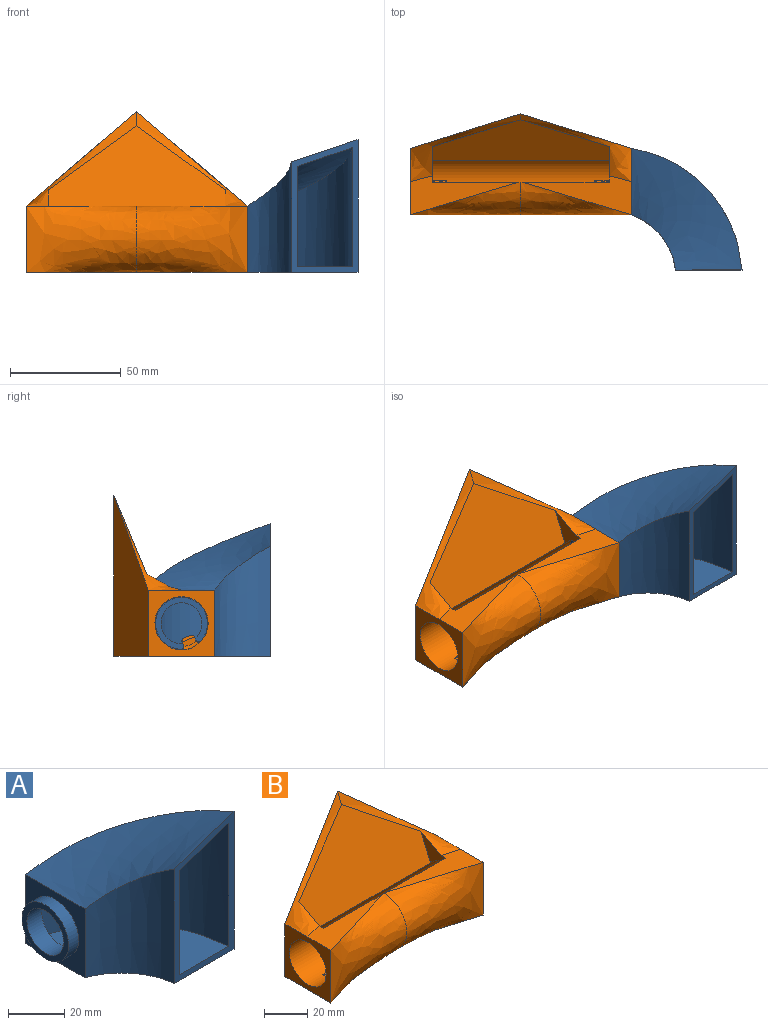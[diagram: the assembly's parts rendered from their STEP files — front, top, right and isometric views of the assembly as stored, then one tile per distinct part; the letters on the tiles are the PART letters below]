
ASSEMBLY  parts=2 mates=1
PART A: 14 faces, bbox 60x60.4x65 mm
  f0: plane 60.52x30.52mm, normal (0,-1,0), area 411.1mm2, adj f2,f3,f4,f5,f9,f10,f11,f12
  f1: plane 30x30mm, normal (-1,0,0), area 466.3mm2, adj f2,f3,f4,f5,f6
  f2: bspline ~50.26x25.43mm, area 1347.3mm2, adj f0,f1,f3,f5
  f3: bspline ~55x50mm, area 1873.7mm2, adj f0,f1,f2,f4
  f4: bspline ~60x55mm, area 3610.5mm2, adj f0,f1,f3,f5
  f5: plane 55x50mm, normal (0,0,-1), area 1683.7mm2, adj f0,f1,f2,f4
  f6: cylinder r=11.75mm len=23.5mm, axis (1,0,0), area 369.1mm2, adj f1,f7
  f7: plane 23.5x23.5mm, normal (-1,0,0), area 164.9mm2, adj f6,f13
  f8: plane 26.26x25.38mm, normal (1,0,0), area 384mm2, adj f9,f10,f11,f12,f13
  f9: offset ~55.26x30.43mm, area 1241.1mm2, adj f0,f8,f10,f12
  f10: offset ~60x55mm, area 1480.6mm2, adj f0,f8,f9,f11
  f11: offset ~65x60mm, area 2913.6mm2, adj f0,f8,f10,f12
  f12: plane 52.63x45.76mm, normal (0,0,1), area 1336.4mm2, adj f0,f8,f9,f11
  f13: cylinder r=9.25mm len=18.5mm, axis (1,0,0), area 435.9mm2, adj f7,f8
PART B: 42 faces, bbox 100x45.5x72.7 mm
  f0: cylinder r=12mm len=100mm, axis (1,0,0), area 6407mm2, adj f4,f9,f12,f13,f14,f15,f34,f35
  f1: bspline ~50x42.69mm, area 363.1mm2, adj f2,f3,f4,f8,f12,f14
  f2: plane 49.17x17.55mm, normal (0,0,1), area 377.9mm2, adj f1,f4,f6,f13,f14
  f3: bspline ~50x42.69mm, area 363.1mm2, adj f1,f5,f9,f11,f12,f15
  f4: plane 30x30mm, normal (-1,0,0), area 447.6mm2, adj f0,f1,f2,f6,f7,f8
  f5: plane 49.17x17.55mm, normal (0,0,1), area 377.9mm2, adj f3,f9,f10,f13,f15
  f6: bspline ~50x30mm, area 1813.5mm2, adj f2,f4,f7,f10,f13
  f7: plane 100x45.54mm, normal (0,0,-1), area 3026.9mm2, adj f4,f6,f8,f9,f10,f11
  f8: plane 72.69x50mm, normal (-0.3,0.95,0), area 2688.4mm2, adj f1,f4,f7,f11
  f9: plane 30x30mm, normal (1,0,0), area 447.6mm2, adj f0,f3,f5,f7,f10,f11
  f10: bspline ~50x30mm, area 1813.5mm2, adj f5,f6,f7,f9,f13
  f11: plane 72.69x50mm, normal (0.3,0.95,0), area 2688.4mm2, adj f3,f7,f8,f9
  f12: plane 80x44mm, normal (0,-0.92,0.38), area 2555.6mm2, adj f0,f1,f3,f14,f15
  f13: plane 80x3.1mm, normal (0,0.92,-0.38), area 268.6mm2, adj f0,f2,f5,f6,f10,f14,f15
  f14: plane 17.32x14.97mm, normal (1,0,0), area 94.3mm2, adj f0,f1,f2,f12,f13
  f15: plane 17.32x14.97mm, normal (-1,0,0), area 94.3mm2, adj f0,f3,f5,f12,f13
  f16: plane 3x1.49mm, normal (0,-0.92,0.38), area 4.9mm2, adj f19,f20,f30,f41
  f17: plane 3x1.49mm, normal (0,0.92,-0.38), area 4.9mm2, adj f19,f20,f33,f38
  f18: plane 3.23x1.35mm, normal (0,0.38,0.92), area 1.8mm2, adj f30,f31,f32,f33
  f19: plane 6.46x4.34mm, normal (1,0,0), area 15mm2, adj f16,f17,f31,f38,f39,f41
  f20: plane 6.46x4.34mm, normal (-1,0,0), area 15mm2, adj f16,f17,f32,f38,f40,f41
  f21: plane 3x1.49mm, normal (0,-0.92,0.38), area 4.9mm2, adj f24,f25,f26,f37
  f22: plane 3x1.49mm, normal (0,0.92,-0.38), area 4.9mm2, adj f24,f25,f29,f34
  f23: plane 3.23x1.35mm, normal (0,0.38,0.92), area 1.8mm2, adj f26,f27,f28,f29
  f24: plane 6.46x4.34mm, normal (-1,0,0), area 15mm2, adj f21,f22,f27,f34,f35,f37
  f25: plane 6.46x4.34mm, normal (1,0,0), area 15mm2, adj f21,f22,f28,f34,f36,f37
  f26: cylinder r=1.25mm len=3mm, axis (-1,0,0), area 4.1mm2, adj f21,f23,f27,f28
  f27: cylinder r=1.25mm len=6.02mm, axis (0,0.92,-0.38), area 9.3mm2, adj f23,f24,f26,f29
  f28: cylinder r=1.25mm len=6.02mm, axis (0,-0.92,0.38), area 9.3mm2, adj f23,f25,f26,f29
  f29: cylinder r=1.25mm len=3mm, axis (1,0,0), area 4.1mm2, adj f22,f23,f27,f28
  f30: cylinder r=1.25mm len=3mm, axis (-1,0,0), area 4.1mm2, adj f16,f18,f31,f32
  f31: cylinder r=1.25mm len=6.02mm, axis (0,0.92,-0.38), area 9.3mm2, adj f18,f19,f30,f33
  f32: cylinder r=1.25mm len=6.02mm, axis (0,-0.92,0.38), area 9.3mm2, adj f18,f20,f30,f33
  f33: cylinder r=1.25mm len=3mm, axis (1,0,0), area 4.1mm2, adj f17,f18,f31,f32
  f34: cylinder r=1.5mm len=6mm, axis (1,0,0), area 12.8mm2, adj f0,f22,f24,f25,f35,f36
  f35: torus R=10.5mm, axis (1,0,0), area 20.1mm2, adj f0,f24,f34,f37
  f36: torus R=10.5mm, axis (1,0,0), area 20.1mm2, adj f0,f25,f34,f37
  f37: cylinder r=1.5mm len=6mm, axis (1,0,0), area 12.8mm2, adj f0,f21,f24,f25,f35,f36
  f38: cylinder r=1.5mm len=6mm, axis (1,0,0), area 12.8mm2, adj f0,f17,f19,f20,f39,f40
  f39: torus R=10.5mm, axis (1,0,0), area 20.1mm2, adj f0,f19,f38,f41
  f40: torus R=10.5mm, axis (1,0,0), area 20.1mm2, adj f0,f20,f38,f41
  f41: cylinder r=1.5mm len=6mm, axis (1,0,0), area 12.8mm2, adj f0,f16,f19,f20,f39,f40
PLACE A t=(55.89,4.21,-4.16)mm
PLACE B t=(5.89,4.21,-4.16)mm
MATE fastened A.f6 <-> B.f0  axis (-1,0,0) through (55.89,4.21,-4.16)mm
